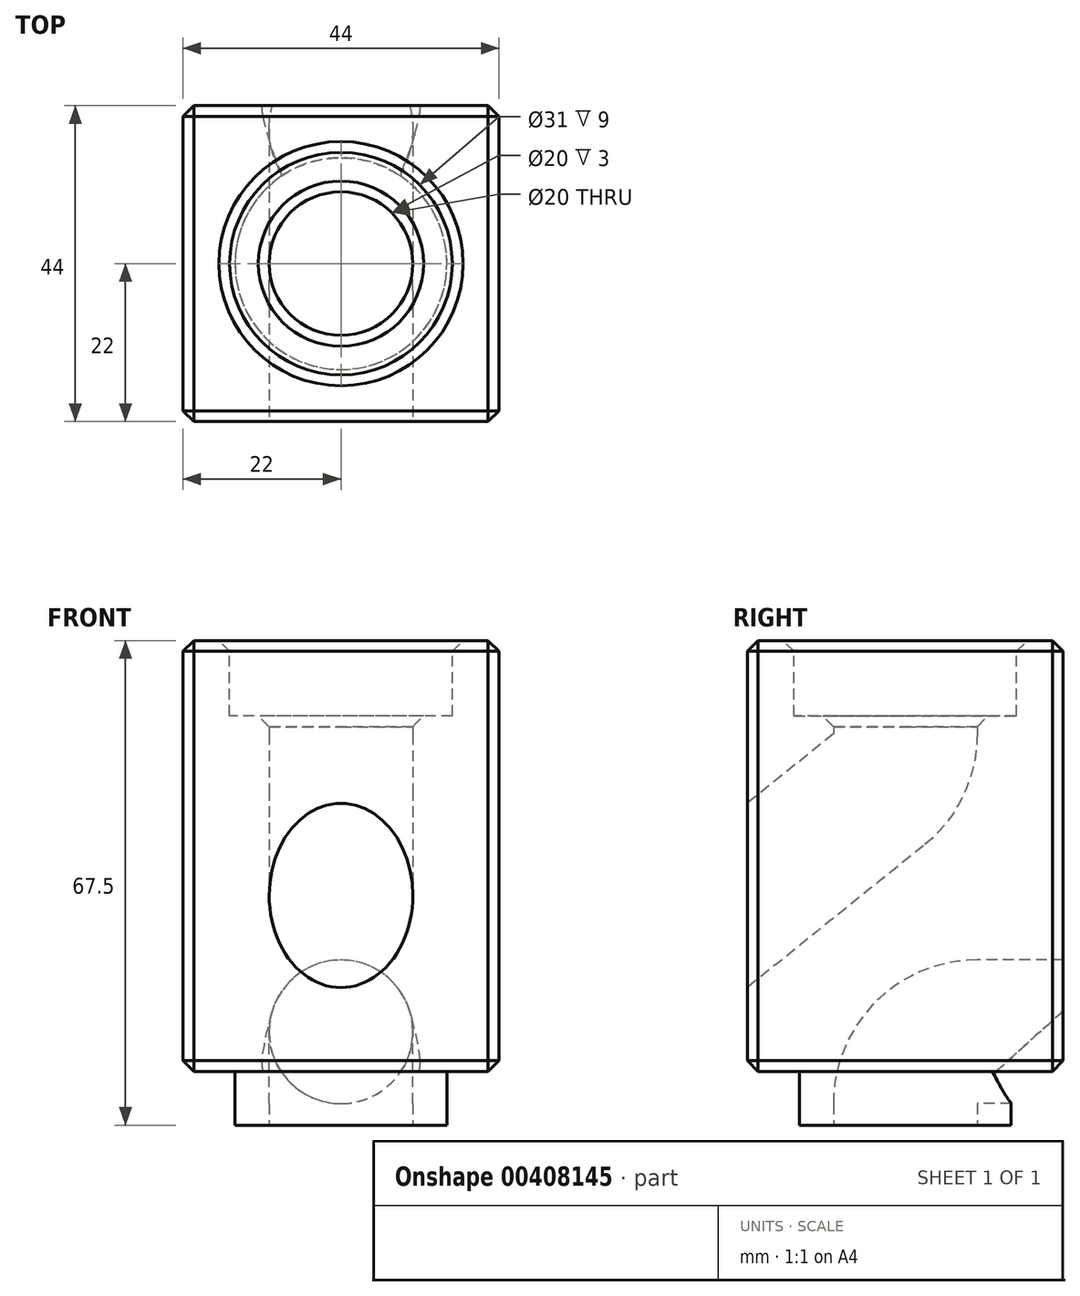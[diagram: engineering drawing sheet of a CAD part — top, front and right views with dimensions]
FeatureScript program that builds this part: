
annotation { "Feature Type Name" : "Feature", "Feature Type Description" : "" }
export const myFeature = defineFeature(function(context is Context, id is Id, definition is map)
    precondition{}
    {
        {
            var Q0;
            Q0=qCreatedBy(makeId("Top.planeOp"),FACE);
            var sketch = newSketch(context, id + "F0", { "sketchPlane" : qUnion([Q0])});
            skLineSegment(sketch, "E0.bottom", {"start": v(-22, 22) * mm, "end": v(22, 22) * mm});
            skLineSegment(sketch, "E0.top", {"start": v(-22, -22) * mm, "end": v(22, -22) * mm});
            skLineSegment(sketch, "E0.left", {"start": v(-22, 22) * mm, "end": v(-22, -22) * mm});
            skLineSegment(sketch, "E0.right", {"start": v(22, 22) * mm, "end": v(22, -22) * mm});
            skSolve(sketch);
        }
        {
            var Q0;
            Q0=makeQuery(id+"F0.imprint","IMPRINT",FACE,{"disambiguationData":[TD([[makeQuery(id+"F0.imprint","IMPRINT",EDGE,{"derivedFrom":sQuery(id+"F0.wireOp",EDGE,"E0.bottom")}),-1.0]])]});
            extrude(context, id + "F1", {"entities" : qUnion([Q0]), "depth" : 60 * mm});
        }
        {
            var Q0;
            Q0=makeQuery(id+"F1.opExtrude","CAP_FACE",FACE,{"disambiguationData":[OSD([sQuery(id+"F0.wireOp",EDGE,"E0.bottom"),sQuery(id+"F0.wireOp",EDGE,"E0.top"),sQuery(id+"F0.wireOp",EDGE,"E0.left"),sQuery(id+"F0.wireOp",EDGE,"E0.right")])],"isStart":true});
            var sketch = newSketch(context, id + "F2", { "sketchPlane" : qUnion([Q0])});
            skCircle(sketch, "E1", {"center": v(0, 0) * mm, "radius": 14.75 * mm});
            skSolve(sketch);
        }
        {
            var Q0;
            Q0=makeQuery(id+"F2.imprint","IMPRINT",FACE,{"disambiguationData":[TD([[makeQuery(id+"F2.imprint","IMPRINT",EDGE,{"derivedFrom":sQuery(id+"F2.wireOp",EDGE,"E1")}),1.0]])]});
            extrude(context, id + "F3", {"entities" : qUnion([Q0]), "operationType" : NewBodyOperationType.ADD, "depth" : 7.5 * mm});
        }
        {
            var Q0;
            Q0=makeQuery(id+"F1.opExtrude","CAP_FACE",FACE,{"disambiguationData":[OSD([sQuery(id+"F0.wireOp",EDGE,"E0.bottom"),sQuery(id+"F0.wireOp",EDGE,"E0.top"),sQuery(id+"F0.wireOp",EDGE,"E0.left"),sQuery(id+"F0.wireOp",EDGE,"E0.right")])],"isStart":false});
            var sketch = newSketch(context, id + "F4", { "sketchPlane" : qUnion([Q0])});
            skCircle(sketch, "E2", {"center": v(0, 0) * mm, "radius": 15.5 * mm});
            skSolve(sketch);
        }
        {
            var Q0;
            Q0=makeQuery(id+"F4.imprint","IMPRINT",FACE,{"disambiguationData":[TD([[makeQuery(id+"F4.imprint","IMPRINT",EDGE,{"derivedFrom":sQuery(id+"F4.wireOp",EDGE,"E2")}),1.0]])]});
            extrude(context, id + "F5", {"entities" : qUnion([Q0]), "operationType" : NewBodyOperationType.REMOVE, "oppositeDirection" : true, "depth" : 10.5 * mm});
        }
        {
            var Q0;
            Q0=makeQuery(id+"F3.opExtrude","CAP_FACE",FACE,{"disambiguationData":[OSD([sQuery(id+"F2.wireOp",EDGE,"E1")])],"isStart":false});
            var sketch = newSketch(context, id + "F6", { "sketchPlane" : qUnion([Q0])});
            skCircle(sketch, "E3", {"center": v(0, 0) * mm, "radius": 9 * mm});
            skSolve(sketch);
        }
        {
            var Q0;
            Q0=makeQuery(id+"F1.opExtrude","SWEPT_FACE",FACE,{"disambiguationData":[OSD([sQuery(id+"F0.wireOp",EDGE,"E0.bottom")])]});
            var sketch = newSketch(context, id + "F7", { "sketchPlane" : qUnion([Q0])});
            skCircle(sketch, "E4", {"center": v(0, 5.5) * mm, "radius": 10 * mm});
            skSolve(sketch);
        }
        {
            var Q0;
            Q0=qCreatedBy(makeId("Right.planeOp"),FACE);
            var sketch = newSketch(context, id + "F8", { "sketchPlane" : qUnion([Q0])});
            skLineSegment(sketch, "E5", {"start": v(22, 5.5) * mm, "end": v(10, 5.5) * mm});
            skLineSegment(sketch, "E6", {"start": v(0, -7.5) * mm, "end": v(0, -4.5) * mm});
            skPoint(sketch, "E7.visualSharp", {"position": v(0, 5.5) * mm});
            skArc(sketch, "E7.filletArc", {"start": v(10, 5.5) * mm, "mid": v(2.93, 2.57) * mm, "end": v(0, -4.5) * mm});
            skSolve(sketch);
        }
        {
            var Q0;
            {var subQ0=sQuery(id+"F7.wireOp",EDGE,"E4");var subQ1=makeQuery(id+"F1.opExtrude","CAP_EDGE",EDGE,{"disambiguationData":[OSD([sQuery(id+"F0.wireOp",EDGE,"E0.bottom")])],"isStart":true});var subQ2=makeQuery(id+"F7.imprint","INTERSECT",VERTEX,{"disambiguationData":[OD(0.0)],"derivedFrom":[subQ1,subQ0]});Q0=makeQuery(id+"F7.imprint","IMPRINT",FACE,{"disambiguationData":[TD([[makeQuery(id+"F7.imprint","IMPRINT",EDGE,{"disambiguationData":[TD([[subQ2,-1.0]])],"derivedFrom":subQ0}),1.0]])]});}
            var Q1;
            {var subQ0=sQuery(id+"F7.wireOp",EDGE,"E4");var subQ1=makeQuery(id+"F1.opExtrude","CAP_EDGE",EDGE,{"disambiguationData":[OSD([sQuery(id+"F0.wireOp",EDGE,"E0.bottom")])],"isStart":true});var subQ2=makeQuery(id+"F7.imprint","INTERSECT",VERTEX,{"disambiguationData":[OD(0.0)],"derivedFrom":[subQ1,subQ0]});Q1=makeQuery(id+"F7.imprint","IMPRINT",FACE,{"disambiguationData":[TD([[makeQuery(id+"F7.imprint","IMPRINT",EDGE,{"disambiguationData":[TD([[subQ2,1.0]])],"derivedFrom":subQ0}),1.0]])]});}
            var Q2;
            Q2=sQuery(id+"F8.wireOp",EDGE,"E6");
            var Q3;
            Q3=sQuery(id+"F8.wireOp",EDGE,"E7.filletArc");
            var Q4;
            Q4=sQuery(id+"F8.wireOp",EDGE,"E5");
            sweep(context, id + "F9", {"operationType" : NewBodyOperationType.REMOVE, "profiles" : qUnion([Q0, Q1]), "path" : qUnion([Q2, Q3, Q4])});
        }
        {
            var Q0;
            Q0=qCreatedBy(makeId("Right.planeOp"),FACE);
            var sketch = newSketch(context, id + "F10", { "sketchPlane" : qUnion([Q0])});
            skLineSegment(sketch, "E8", {"start": v(-3.73, 39.21) * mm, "end": v(-22, 24.5) * mm});
            skLineSegment(sketch, "E9", {"start": v(0, 47) * mm, "end": v(0, 60) * mm});
            skPoint(sketch, "E10.visualSharp", {"position": v(0, 42.21) * mm});
            skArc(sketch, "E10.filletArc", {"start": v(-3.73, 39.21) * mm, "mid": v(-0.98, 42.68) * mm, "end": v(0, 47) * mm});
            skLineSegment(sketch, "E11", {"start": v(-22, 24.5) * mm, "end": v(-43.35, 7.31) * mm});
            skSolve(sketch);
        }
        {
            var Q0;
            Q0=makeQuery(id+"F4.imprint","IMPRINT",FACE,{"disambiguationData":[TD([[makeQuery(id+"F4.imprint","IMPRINT",EDGE,{"derivedFrom":sQuery(id+"F4.wireOp",EDGE,"E2")}),-1.0]])]});
            var sketch = newSketch(context, id + "F11", { "sketchPlane" : qUnion([Q0])});
            skCircle(sketch, "E12", {"center": v(0, 0) * mm, "radius": 10 * mm});
            skSolve(sketch);
        }
        {
            var Q0;
            Q0=makeQuery(id+"F11.imprint","IMPRINT",FACE,{"disambiguationData":[TD([[makeQuery(id+"F11.imprint","IMPRINT",EDGE,{"derivedFrom":sQuery(id+"F11.wireOp",EDGE,"E12")}),1.0]])]});
            var Q1;
            Q1=sQuery(id+"F10.wireOp",EDGE,"E9");
            var Q2;
            Q2=sQuery(id+"F10.wireOp",EDGE,"E10.filletArc");
            var Q3;
            Q3=sQuery(id+"F10.wireOp",EDGE,"E8");
            var Q4;
            Q4=sQuery(id+"F10.wireOp",EDGE,"E11");
            sweep(context, id + "F12", {"operationType" : NewBodyOperationType.REMOVE, "profiles" : qUnion([Q0]), "path" : qUnion([Q1, Q2, Q3, Q4])});
        }
        {
            var Q0;
            Q0=makeQuery(id+"F1.opExtrude","CAP_FACE",FACE,{"disambiguationData":[OSD([sQuery(id+"F0.wireOp",EDGE,"E0.bottom"),sQuery(id+"F0.wireOp",EDGE,"E0.top"),sQuery(id+"F0.wireOp",EDGE,"E0.left"),sQuery(id+"F0.wireOp",EDGE,"E0.right")])],"isStart":false});
            var Q1;
            Q1=makeQuery(id+"F1.opExtrude","SWEPT_FACE",FACE,{"disambiguationData":[OSD([sQuery(id+"F0.wireOp",EDGE,"E0.right")])]});
            var Q2;
            {var subQ0=sQuery(id+"F0.wireOp",EDGE,"E0.bottom");var subQ1=sQuery(id+"F0.wireOp",EDGE,"E0.right");Q2=makeQuery(id+"F9.boolean.opBoolean","SPLIT",EDGE,{"disambiguationData":[TD([makeQuery(id+"F1.opExtrude","SWEPT_FACE",FACE,{"disambiguationData":[OSD([subQ1])]})])],"derivedFrom":makeQuery(id+"F1.opExtrude","CAP_EDGE",EDGE,{"disambiguationData":[OSD([subQ0])],"isStart":true})});}
            var Q3;
            {var subQ0=sQuery(id+"F0.wireOp",EDGE,"E0.bottom");var subQ1=sQuery(id+"F0.wireOp",EDGE,"E0.left");Q3=makeQuery(id+"F9.boolean.opBoolean","SPLIT",EDGE,{"disambiguationData":[TD([makeQuery(id+"F1.opExtrude","SWEPT_FACE",FACE,{"disambiguationData":[OSD([subQ1])]})])],"derivedFrom":makeQuery(id+"F1.opExtrude","CAP_EDGE",EDGE,{"disambiguationData":[OSD([subQ0])],"isStart":true})});}
            var Q4;
            Q4=makeQuery(id+"F1.opExtrude","SWEPT_FACE",FACE,{"disambiguationData":[OSD([sQuery(id+"F0.wireOp",EDGE,"E0.left")])]});
            var Q5;
            Q5=makeQuery(id+"F1.opExtrude","CAP_EDGE",EDGE,{"disambiguationData":[OSD([sQuery(id+"F0.wireOp",EDGE,"E0.top")])],"isStart":true});
            var Q6;
            Q6=makeQuery(id+"F12.boolean.opBoolean","INTERSECT",EDGE,{"derivedFrom":[makeQuery(id+"F5.boolean.opBoolean","COPY",FACE,{"derivedFrom":makeQuery(id+"F5.opExtrude","CAP_FACE",FACE,{"disambiguationData":[OSD([sQuery(id+"F4.wireOp",EDGE,"E2")])],"isStart":false})}),makeQuery(id+"F12.opSweep","SWEPT_FACE",FACE,{"disambiguationData":[OSD([sQuery(id+"F10.wireOp",EDGE,"E9"),sQuery(id+"F11.wireOp",EDGE,"E12")])]})]});
            chamfer(context, id + "F13", {"entities" : qUnion([Q0, Q1, Q2, Q3, Q4, Q5, Q6]), "width" : 1.5 * mm, "tangentPropagation" : true});
        }
        {
            var Q0;
            {var subQ0=makeQuery(id+"F9.opSweep","SWEPT_FACE",FACE,{"disambiguationData":[OSD([sQuery(id+"F7.wireOp",EDGE,"E4"),sQuery(id+"F8.wireOp",EDGE,"E5")])]});var subQ1=sQuery(id+"F0.wireOp",EDGE,"E0.bottom");var subQ2=sQuery(id+"F0.wireOp",EDGE,"E0.left");Q0=makeQuery(id+"F13.opChamfer","BLEND_EDGE",EDGE,{"blendedFrom":[makeQuery(id+"F9.boolean.opBoolean","SPLIT",EDGE,{"disambiguationData":[TD([makeQuery(id+"F1.opExtrude","SWEPT_FACE",FACE,{"disambiguationData":[OSD([subQ2])]})])],"derivedFrom":makeQuery(id+"F1.opExtrude","CAP_EDGE",EDGE,{"disambiguationData":[OSD([subQ1])],"isStart":true})}),makeQuery(id+"F9.boolean.opBoolean","COPY",FACE,{"derivedFrom":subQ0})],"blendedInto":[makeQuery(id+"F9.boolean.opBoolean","COPY",FACE,{"derivedFrom":subQ0})]});}
            var Q1;
            {var subQ0=makeQuery(id+"F9.opSweep","SWEPT_FACE",FACE,{"disambiguationData":[OSD([sQuery(id+"F7.wireOp",EDGE,"E4"),sQuery(id+"F8.wireOp",EDGE,"E5")])]});var subQ1=sQuery(id+"F0.wireOp",EDGE,"E0.bottom");var subQ2=sQuery(id+"F0.wireOp",EDGE,"E0.right");Q1=makeQuery(id+"F13.opChamfer","BLEND_EDGE",EDGE,{"blendedFrom":[makeQuery(id+"F9.boolean.opBoolean","SPLIT",EDGE,{"disambiguationData":[TD([makeQuery(id+"F1.opExtrude","SWEPT_FACE",FACE,{"disambiguationData":[OSD([subQ2])]})])],"derivedFrom":makeQuery(id+"F1.opExtrude","CAP_EDGE",EDGE,{"disambiguationData":[OSD([subQ1])],"isStart":true})}),makeQuery(id+"F9.boolean.opBoolean","COPY",FACE,{"derivedFrom":subQ0})],"blendedInto":[makeQuery(id+"F9.boolean.opBoolean","COPY",FACE,{"derivedFrom":subQ0})]});}
            chamfer(context, id + "F14", {"entities" : qUnion([Q0, Q1]), "chamferType" : ChamferType.OFFSET_ANGLE, "width" : 6 * mm, "oppositeDirection" : false, "angle" : 33 * degree, "tangentPropagation" : true});
        }
    });
